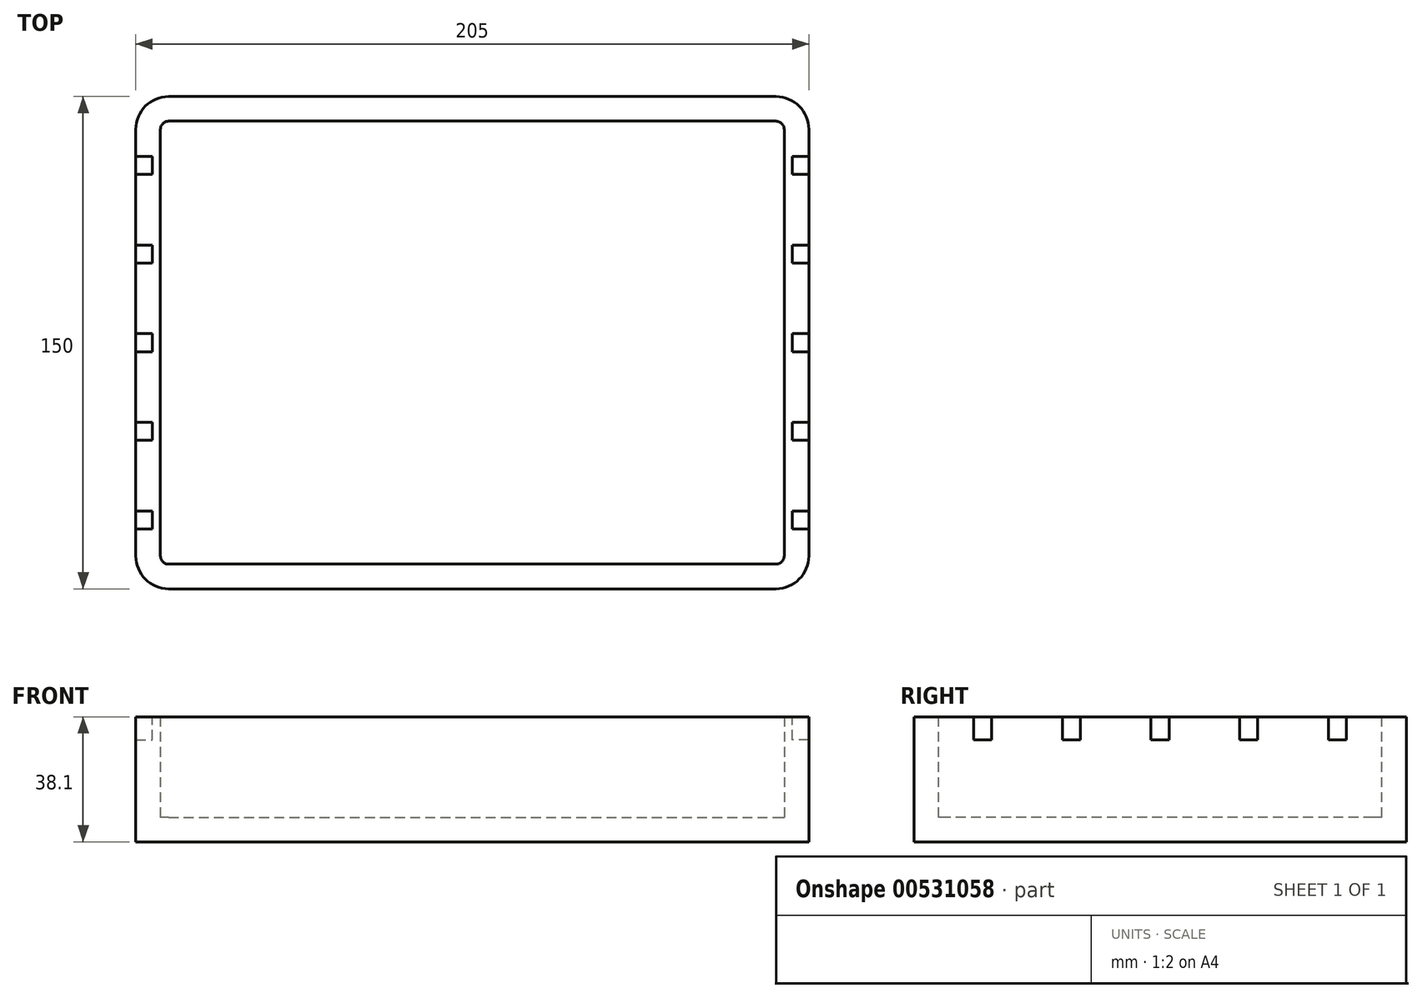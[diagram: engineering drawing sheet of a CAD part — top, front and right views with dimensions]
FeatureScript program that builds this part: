
annotation { "Feature Type Name" : "Feature", "Feature Type Description" : "" }
export const myFeature = defineFeature(function(context is Context, id is Id, definition is map)
    precondition{}
    {
        {
            var Q0;
            Q0=qCreatedBy(makeId("Top.planeOp"),FACE);
            var sketch = newSketch(context, id + "F0", { "sketchPlane" : qUnion([Q0])});
            skLineSegment(sketch, "E0.bottom", {"start": v(-92.5, 63.3) * mm, "end": v(92.5, 63.3) * mm});
            skLineSegment(sketch, "E0.top", {"start": v(-92.5, -86.7) * mm, "end": v(92.5, -86.7) * mm});
            skLineSegment(sketch, "E0.left", {"start": v(-102.5, 53.3) * mm, "end": v(-102.5, -76.7) * mm});
            skLineSegment(sketch, "E0.right", {"start": v(102.5, 53.3) * mm, "end": v(102.5, -76.7) * mm});
            skPoint(sketch, "E1.visualSharp", {"position": v(-102.5, -86.7) * mm});
            skArc(sketch, "E1.filletArc", {"start": v(-102.5, -76.7) * mm, "mid": v(-99.57, -83.78) * mm, "end": v(-92.5, -86.7) * mm});
            skPoint(sketch, "E2.visualSharp", {"position": v(-102.5, 63.3) * mm});
            skArc(sketch, "E2.filletArc", {"start": v(-92.5, 63.3) * mm, "mid": v(-99.57, 60.36) * mm, "end": v(-102.5, 53.3) * mm});
            skPoint(sketch, "E3.visualSharp", {"position": v(102.5, 63.3) * mm});
            skArc(sketch, "E3.filletArc", {"start": v(102.5, 53.3) * mm, "mid": v(99.57, 60.36) * mm, "end": v(92.5, 63.3) * mm});
            skPoint(sketch, "E4.visualSharp", {"position": v(102.5, -86.7) * mm});
            skArc(sketch, "E4.filletArc", {"start": v(92.5, -86.7) * mm, "mid": v(99.57, -83.78) * mm, "end": v(102.5, -76.7) * mm});
            skSolve(sketch);
        }
        {
            var Q0;
            Q0 = qSketchRegion(id + "F0", true);
            extrude(context, id + "F1", {"entities" : qUnion([Q0]), "depth" : 38.1 * mm, "offsetDistance" : 25 * mm});
        }
        {
            var Q0;
            Q0=makeQuery(id+"F1.opExtrude","CAP_FACE",FACE,{"disambiguationData":[OSD([sQuery(id+"F0.wireOp",EDGE,"E0.bottom"),sQuery(id+"F0.wireOp",EDGE,"E0.top"),sQuery(id+"F0.wireOp",EDGE,"E0.left"),sQuery(id+"F0.wireOp",EDGE,"E0.right")])],"isStart":false});
            shell(context, id + "F2", {"entities" : qUnion([Q0]), "thickness" : 7.5 * mm});
        }
        {
            var Q0;
            Q0=makeQuery(id+"F1.opExtrude","CAP_FACE",FACE,{"disambiguationData":[OSD([sQuery(id+"F0.wireOp",EDGE,"E0.bottom"),sQuery(id+"F0.wireOp",EDGE,"E0.top"),sQuery(id+"F0.wireOp",EDGE,"E0.left"),sQuery(id+"F0.wireOp",EDGE,"E0.right")])],"isStart":false});
            var sketch = newSketch(context, id + "F3", { "sketchPlane" : qUnion([Q0])});
            skLineSegment(sketch, "E5.bottom", {"start": v(-102.5, 45.04) * mm, "end": v(-97.5, 45.04) * mm});
            skLineSegment(sketch, "E5.top", {"start": v(-102.5, 39.54) * mm, "end": v(-97.5, 39.54) * mm});
            skLineSegment(sketch, "E5.left", {"start": v(-102.5, 45.04) * mm, "end": v(-102.5, 39.54) * mm});
            skLineSegment(sketch, "E5.right", {"start": v(-97.5, 45.04) * mm, "end": v(-97.5, 39.54) * mm});
            skLineSegment(sketch, "E6.bottom", {"start": v(-102.5, -8.96) * mm, "end": v(-97.5, -8.96) * mm});
            skLineSegment(sketch, "E6.top", {"start": v(-102.5, -14.5) * mm, "end": v(-97.5, -14.5) * mm});
            skLineSegment(sketch, "E6.left", {"start": v(-102.5, -8.96) * mm, "end": v(-102.5, -14.5) * mm});
            skLineSegment(sketch, "E6.right", {"start": v(-97.5, -8.96) * mm, "end": v(-97.5, -14.5) * mm});
            skPoint(sketch, "E7.oppositeSnap0", {"position": v(-97.5, -38.7) * mm});
            skLineSegment(sketch, "E7.bottom", {"start": v(-102.5, -35.96) * mm, "end": v(-97.5, -35.96) * mm});
            skLineSegment(sketch, "E7.top", {"start": v(-102.5, -41.46) * mm, "end": v(-97.5, -41.46) * mm});
            skLineSegment(sketch, "E7.left", {"start": v(-102.5, -35.96) * mm, "end": v(-102.5, -41.46) * mm});
            skLineSegment(sketch, "E7.right", {"start": v(-97.5, -35.96) * mm, "end": v(-97.5, -41.46) * mm});
            skLineSegment(sketch, "E8.bottom", {"start": v(-102.5, -62.96) * mm, "end": v(-97.5, -62.96) * mm});
            skLineSegment(sketch, "E8.top", {"start": v(-102.5, -68.46) * mm, "end": v(-97.5, -68.46) * mm});
            skLineSegment(sketch, "E8.left", {"start": v(-102.5, -62.96) * mm, "end": v(-102.5, -68.46) * mm});
            skLineSegment(sketch, "E8.right", {"start": v(-97.5, -62.96) * mm, "end": v(-97.5, -68.46) * mm});
            skLineSegment(sketch, "E9.bottom", {"start": v(-102.5, 18.04) * mm, "end": v(-97.5, 18.04) * mm});
            skLineSegment(sketch, "E9.top", {"start": v(-102.5, 12.54) * mm, "end": v(-97.5, 12.54) * mm});
            skLineSegment(sketch, "E9.left", {"start": v(-102.5, 18.04) * mm, "end": v(-102.5, 12.54) * mm});
            skLineSegment(sketch, "E9.right", {"start": v(-97.5, 18.04) * mm, "end": v(-97.5, 12.54) * mm});
            skLineSegment(sketch, "E10.MirrorCS", {"start": v(102.5, 45.04) * mm, "end": v(97.5, 45.04) * mm});
            skLineSegment(sketch, "E11.MirrorCS", {"start": v(102.5, 45.04) * mm, "end": v(102.5, 39.54) * mm});
            skLineSegment(sketch, "E12.MirrorCS", {"start": v(102.5, 39.54) * mm, "end": v(97.5, 39.54) * mm});
            skLineSegment(sketch, "E13.MirrorCS", {"start": v(97.5, 45.04) * mm, "end": v(97.5, 39.54) * mm});
            skLineSegment(sketch, "E14.MirrorCS", {"start": v(102.5, 12.54) * mm, "end": v(97.5, 12.54) * mm});
            skLineSegment(sketch, "E15.MirrorCS", {"start": v(97.5, 18.04) * mm, "end": v(97.5, 12.54) * mm});
            skLineSegment(sketch, "E16.MirrorCS", {"start": v(102.5, 18.04) * mm, "end": v(97.5, 18.04) * mm});
            skLineSegment(sketch, "E17.MirrorCS", {"start": v(102.5, 18.04) * mm, "end": v(102.5, 12.54) * mm});
            skLineSegment(sketch, "E18.MirrorCS", {"start": v(102.5, -8.96) * mm, "end": v(97.5, -8.96) * mm});
            skLineSegment(sketch, "E19.MirrorCS", {"start": v(102.5, -8.96) * mm, "end": v(102.5, -14.5) * mm});
            skLineSegment(sketch, "E20.MirrorCS", {"start": v(102.5, -14.5) * mm, "end": v(97.5, -14.5) * mm});
            skLineSegment(sketch, "E21.MirrorCS", {"start": v(97.5, -8.96) * mm, "end": v(97.5, -14.5) * mm});
            skLineSegment(sketch, "E22.MirrorCS", {"start": v(102.5, -35.96) * mm, "end": v(97.5, -35.96) * mm});
            skLineSegment(sketch, "E23.MirrorCS", {"start": v(102.5, -41.46) * mm, "end": v(97.5, -41.46) * mm});
            skLineSegment(sketch, "E24.MirrorCS", {"start": v(97.5, -35.96) * mm, "end": v(97.5, -41.46) * mm});
            skLineSegment(sketch, "E25.MirrorCS", {"start": v(102.5, -35.96) * mm, "end": v(102.5, -41.46) * mm});
            skLineSegment(sketch, "E26.MirrorCS", {"start": v(102.5, -62.96) * mm, "end": v(97.5, -62.96) * mm});
            skLineSegment(sketch, "E27.MirrorCS", {"start": v(97.5, -62.96) * mm, "end": v(97.5, -68.46) * mm});
            skLineSegment(sketch, "E28.MirrorCS", {"start": v(102.5, -68.46) * mm, "end": v(97.5, -68.46) * mm});
            skLineSegment(sketch, "E29.MirrorCS", {"start": v(102.5, -62.96) * mm, "end": v(102.5, -68.46) * mm});
            skLineSegment(sketch, "E30", {"start": v(-102.5, 42.3) * mm, "end": v(-97.5, 42.3) * mm, "construction": true});
            skLineSegment(sketch, "E31", {"start": v(-102.5, 15.3) * mm, "end": v(-97.5, 15.3) * mm, "construction": true});
            skLineSegment(sketch, "E32", {"start": v(-102.5, -11.7) * mm, "end": v(-97.5, -11.7) * mm, "construction": true});
            skLineSegment(sketch, "E33", {"start": v(-102.5, -38.7) * mm, "end": v(-97.5, -38.7) * mm, "construction": true});
            skLineSegment(sketch, "E34", {"start": v(-102.5, -65.7) * mm, "end": v(-97.5, -65.7) * mm, "construction": true});
            skSolve(sketch);
        }
        {
            var Q0;
            Q0=makeQuery(id+"F3.imprint","IMPRINT",FACE,{"disambiguationData":[TD([[makeQuery(id+"F3.imprint","IMPRINT",EDGE,{"derivedFrom":sQuery(id+"F3.wireOp",EDGE,"E5.bottom")}),-1.0]])]});
            var Q1;
            Q1=makeQuery(id+"F3.imprint","IMPRINT",FACE,{"disambiguationData":[TD([[makeQuery(id+"F3.imprint","IMPRINT",EDGE,{"derivedFrom":sQuery(id+"F3.wireOp",EDGE,"E9.bottom")}),-1.0]])]});
            var Q2;
            Q2=makeQuery(id+"F3.imprint","IMPRINT",FACE,{"disambiguationData":[TD([[makeQuery(id+"F3.imprint","IMPRINT",EDGE,{"derivedFrom":sQuery(id+"F3.wireOp",EDGE,"E6.bottom")}),-1.0]])]});
            var Q3;
            Q3=makeQuery(id+"F3.imprint","IMPRINT",FACE,{"disambiguationData":[TD([[makeQuery(id+"F3.imprint","IMPRINT",EDGE,{"derivedFrom":sQuery(id+"F3.wireOp",EDGE,"E7.bottom")}),-1.0]])]});
            var Q4;
            Q4=makeQuery(id+"F3.imprint","IMPRINT",FACE,{"disambiguationData":[TD([[makeQuery(id+"F3.imprint","IMPRINT",EDGE,{"derivedFrom":sQuery(id+"F3.wireOp",EDGE,"E8.bottom")}),-1.0]])]});
            var Q5;
            Q5=makeQuery(id+"F3.imprint","IMPRINT",FACE,{"disambiguationData":[TD([[makeQuery(id+"F3.imprint","IMPRINT",EDGE,{"derivedFrom":sQuery(id+"F3.wireOp",EDGE,"E26.MirrorCS")}),1.0]])]});
            var Q6;
            Q6=makeQuery(id+"F3.imprint","IMPRINT",FACE,{"disambiguationData":[TD([[makeQuery(id+"F3.imprint","IMPRINT",EDGE,{"derivedFrom":sQuery(id+"F3.wireOp",EDGE,"E22.MirrorCS")}),1.0]])]});
            var Q7;
            Q7=makeQuery(id+"F3.imprint","IMPRINT",FACE,{"disambiguationData":[TD([[makeQuery(id+"F3.imprint","IMPRINT",EDGE,{"derivedFrom":sQuery(id+"F3.wireOp",EDGE,"E18.MirrorCS")}),1.0]])]});
            var Q8;
            Q8=makeQuery(id+"F3.imprint","IMPRINT",FACE,{"disambiguationData":[TD([[makeQuery(id+"F3.imprint","IMPRINT",EDGE,{"derivedFrom":sQuery(id+"F3.wireOp",EDGE,"E14.MirrorCS")}),-1.0]])]});
            var Q9;
            Q9=makeQuery(id+"F3.imprint","IMPRINT",FACE,{"disambiguationData":[TD([[makeQuery(id+"F3.imprint","IMPRINT",EDGE,{"derivedFrom":sQuery(id+"F3.wireOp",EDGE,"E10.MirrorCS")}),1.0]])]});
            extrude(context, id + "F4", {"entities" : qUnion([Q0, Q1, Q2, Q3, Q4, Q5, Q6, Q7, Q8, Q9]), "operationType" : NewBodyOperationType.REMOVE, "oppositeDirection" : true, "depth" : 7 * mm, "offsetDistance" : 25 * mm});
        }
    });
